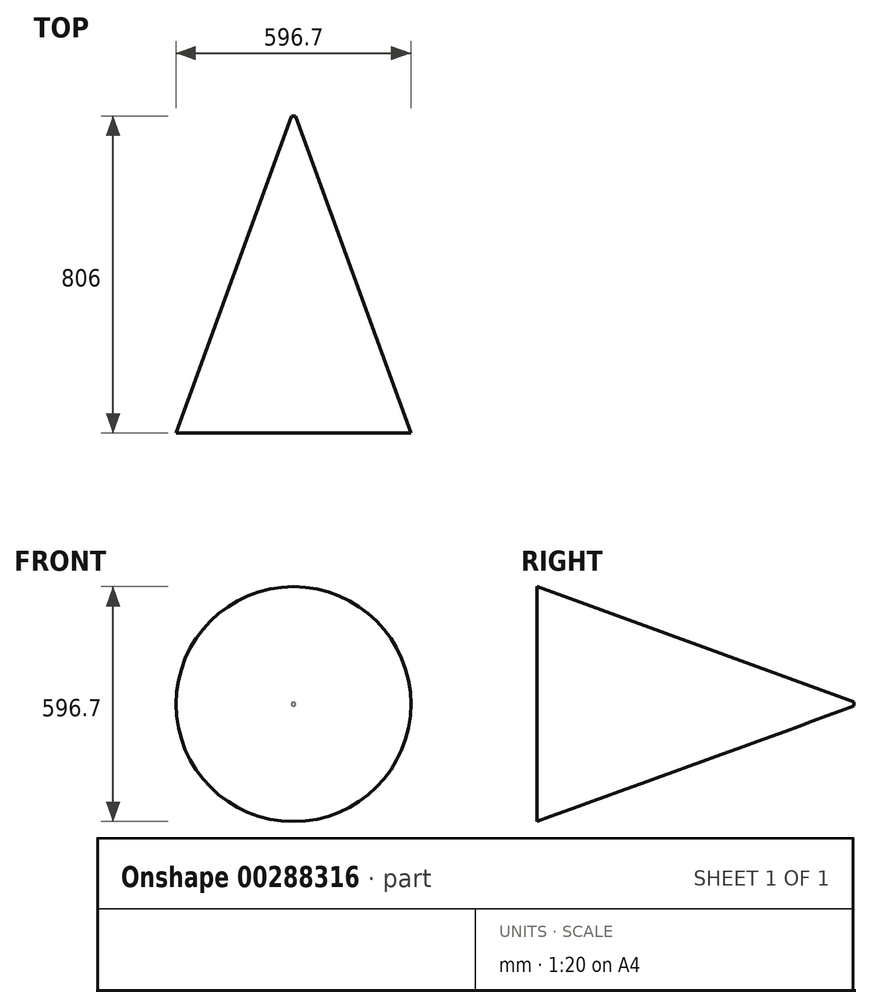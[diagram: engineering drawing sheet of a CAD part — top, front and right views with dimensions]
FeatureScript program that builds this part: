
annotation { "Feature Type Name" : "Feature", "Feature Type Description" : "" }
export const myFeature = defineFeature(function(context is Context, id is Id, definition is map)
    precondition{}
    {
        {
            var Q0;
            Q0=qCreatedBy(makeId("Front.planeOp"),FACE);
            var sketch = newSketch(context, id + "F0", { "sketchPlane" : qUnion([Q0])});
            skCircle(sketch, "E0", {"center": v(0, 0) * mm, "radius": 5 * mm});
            skSolve(sketch);
        }
        {
            var Q0;
            Q0=makeQuery(id+"F0.imprint","IMPRINT",FACE,{"disambiguationData":[TD([[makeQuery(id+"F0.imprint","IMPRINT",EDGE,{"derivedFrom":sQuery(id+"F0.wireOp",EDGE,"E0")}),1.0]])]});
            extrude(context, id + "F1", {"entities" : qUnion([Q0]), "depth" : 806 * mm, "hasDraft" : true, "draftAngle" : 20 * degree});
        }
    });
